# Revit family: NLRS_63_LF_LUM-DL20LT-xxxx_luminaid
name_source: partatom
category: Lighting Fixtures
revit_build: Autodesk Revit 2018 (Build: 20190510_1515(x64)
units: mm (PartAtom-declared; Revit-internal decimal feet)

## family parameters
Always vertical = Yes
Cut with Voids When Loaded = No
Light Source = Yes
Part Type = Normal
Room Calculation Point = No
Round Connector Dimension = Use Diameter
Shared = No
Work Plane-Based = No

## types (18) — shared parameters
Ambient temp range = -20°C±40°C
Certification = ENEC, CE
Color Filter = 16777215
Diameter = 40 mm  [stored 0.131234 ft]
Diming = 0-10 V – 0-100%
Dimming Lamp Color Temperature Shift = <None>
Emit from Line Length = 2038 mm  [stored 6.68635 ft]
Housing Material = Polycarbonate
Housing- IP = IP65
Impact Protection Rating-IK = IK10
Input Voltage & frequency = 200-250, 50 Hz
Length = 2038 mm  [stored 6.68635 ft]
Manufacturer = LUMINAID B.V.
Middle Support = No
Product Brand = DATALUX.LT
Side Support = No
Support Distance = 1019 mm
Tilt Angle = 90.00°
Tube Offset = 20 mm  [stored 0.0656168 ft]
Weight = 2.20 kg

## per-type parameters (varying)
| type | Lens type | Lumen | Photometric Web File | Power |
| LUM-DL20LT-NAxx-02K5 | Narrow beam | 1800 lm | LUM-DL20LT-NAxx-02K5.ies | 11 W |
| LUM-DL20LT-WAxx-02K5 | Wide beam | 1880 lm | LUM-DL20LT-WAxx-02K5.ies | 11 W |
| LUM-DL20LT-UWxx-02K5 | Ultrawide beam | 1690 lm | LUM-DL20LT-UWxx-02K5.ies | 11 W |
| LUM-DL20LT-NAxx-03K5 | Narrow beam | 2510 lm | LUM-DL20LT-NAxx-03K5.ies | 16 W |
| LUM-DL20LT-WAxx-03K5 | Wide beam | 2620 lm | LUM-DL20LT-WAxx-03K5.ies | 16 W |
| LUM-DL20LT-UWxx-03K5 | Ultrawide beam | 2350 lm | LUM-DL20LT-UWxx-03K5.ies | 16 W |
| LUM-DL20LT-NAxx-05K0 | Narrow beam | 3580 lm | LUM-DL20LT-NAxx-05K0.ies | 23 W |
| LUM-DL20LT-WAxx-05K0 | Wide beam | 3740 lm | LUM-DL20LT-WAxx-05K0.ies | 23 W |
| LUM-DL20LT-UWxx-05K0 | Ultrawide beam | 3360 lm | LUM-DL20LT-UWxx-05K0.ies | 23 W |
| LUM-DL20LT-NAxx-06K5 | Narrow beam | 4650 lm | LUM-DL20LT-NAxx-06K5.ies | 31 W |
| LUM-DL20LT-WAxx-06K5 | Wide beam | 4920 lm | LUM-DL20LT-WAxx-06K5.ies | 31 W |
| LUM-DL20LT-UWxx-06K5 | Ultrawide beam | 4420 lm | LUM-DL20LT-UWxx-06K5.ies | 31 W |
| LUM-DL20LT-NAxx-08K0 | Narrow beam | 5830 lm | LUM-DL20LT-NAxx-08K0.ies | 36 W |
| LUM-DL20LT-WAxx-08K0 | Wide beam | 6070 lm | LUM-DL20LT-WAxx-08K0.ies | 36 W |
| LUM-DL20LT-UWxx-08K0 | Ultrawide beam | 5500 lm | LUM-DL20LT-UWxx-08K0.ies | 36 W |
| LUM-DL20LT-NAxx-12K0 | Narrow beam | 7700 lm | LUM-DL20LT-NAxx-12K0.ies | 50 W |
| LUM-DL20LT-WAxx-12K0 | Wide beam | 8040 lm | LUM-DL20LT-WAxx-12K0.ies | 50 W |
| LUM-DL20LT-UWxx-12K0 | Ultrawide beam | 7260 lm | LUM-DL20LT-UWxx-12K0.ies | 50 W |

note: column(s) folded — value = type name in every type: Article code

note: [stored X ft] marks values corroborated as IEEE doubles in the binary element streams (Revit-internal decimal feet)

## geometry (parser evidence)
native form markers: Sweep x15
no freeform markers — native parametric forms only
